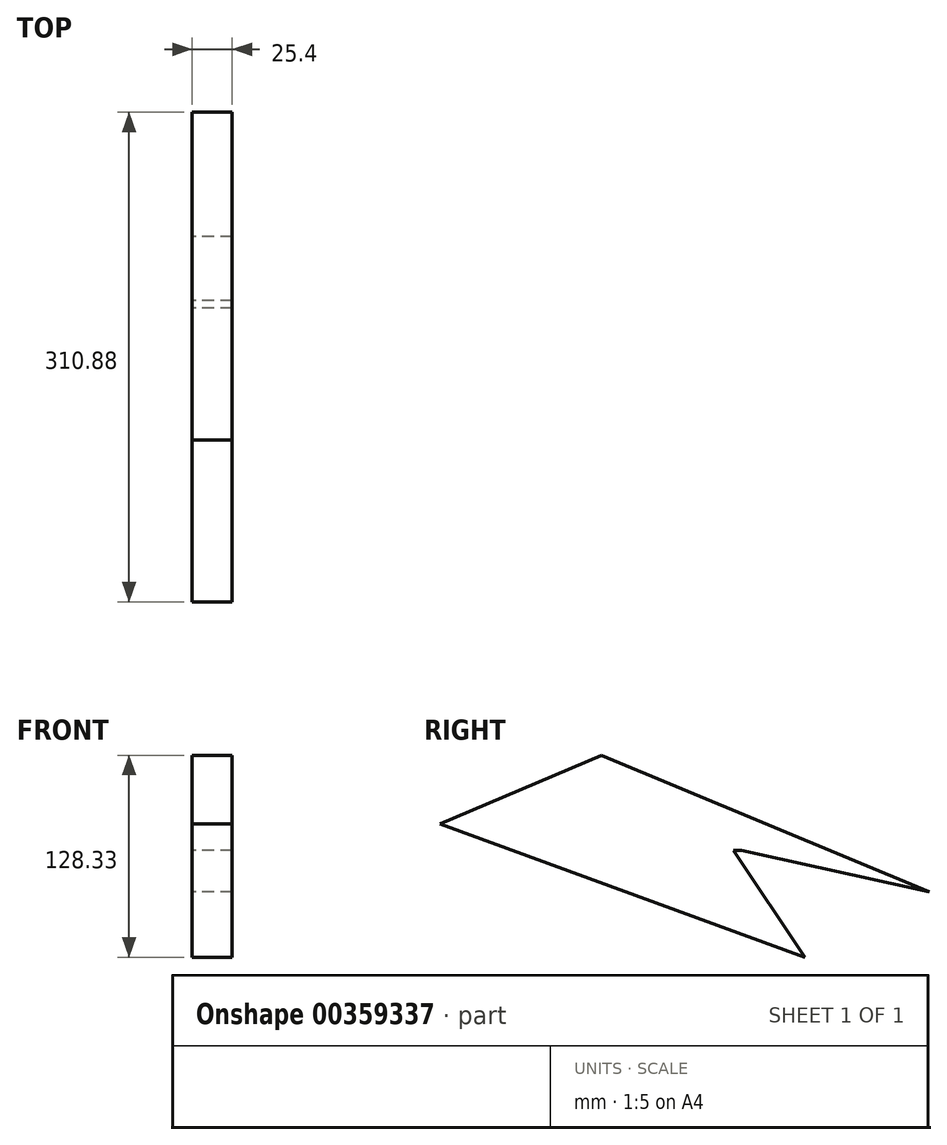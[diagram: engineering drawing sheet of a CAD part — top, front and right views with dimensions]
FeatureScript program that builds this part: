
annotation { "Feature Type Name" : "Feature", "Feature Type Description" : "" }
export const myFeature = defineFeature(function(context is Context, id is Id, definition is map)
    precondition{}
    {
        {
            var Q0;
            Q0=qCreatedBy(makeId("Right.planeOp"),FACE);
            var sketch = newSketch(context, id + "F0", { "sketchPlane" : qUnion([Q0])});
            skLineSegment(sketch, "E0", {"start": v(-78.84, 31.07) * mm, "end": v(-124.28, 99.11) * mm});
            skLineSegment(sketch, "E1", {"start": v(-119.46, 99.09) * mm, "end": v(0, 72.47) * mm});
            skLineSegment(sketch, "E2", {"start": v(0, 72.47) * mm, "end": v(-208.29, 159.4) * mm});
            skLineSegment(sketch, "E3", {"start": v(-208.29, 159.4) * mm, "end": v(-310.88, 115.69) * mm});
            skLineSegment(sketch, "E4", {"start": v(-310.88, 115.69) * mm, "end": v(-78.84, 31.07) * mm});
            skLineSegment(sketch, "E5", {"start": v(-124.28, 99.11) * mm, "end": v(-119.46, 99.09) * mm});
            skSolve(sketch);
        }
        {
            var Q0;
            Q0=makeQuery(id+"F0.imprint","IMPRINT",FACE,{"disambiguationData":[TD([[makeQuery(id+"F0.imprint","IMPRINT",EDGE,{"derivedFrom":sQuery(id+"F0.wireOp",EDGE,"E0")}),1.0]])]});
            extrude(context, id + "F1", {"entities" : qUnion([Q0]), "depth" : 25.4 * mm});
        }
    });
